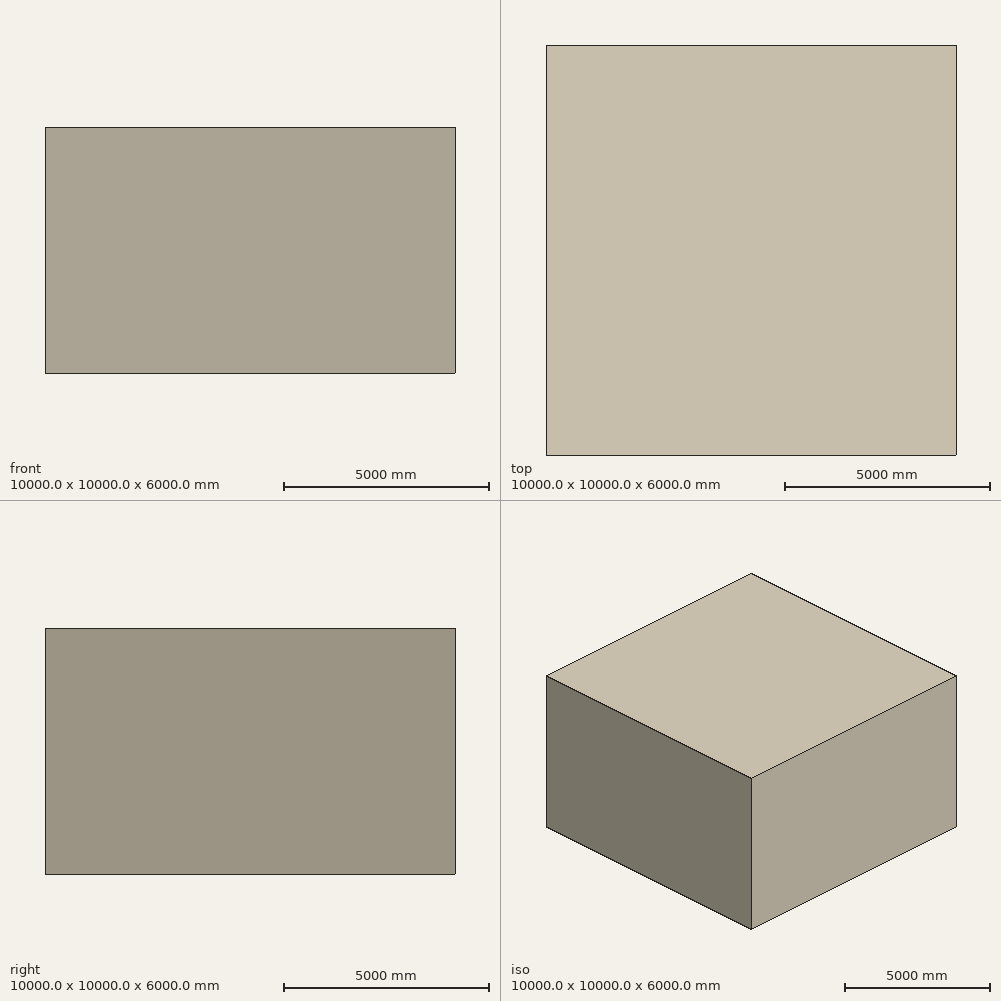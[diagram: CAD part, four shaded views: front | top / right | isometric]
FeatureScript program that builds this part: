
annotation { "Feature Type Name" : "Feature", "Feature Type Description" : "" }
export const myFeature = defineFeature(function(context is Context, id is Id, definition is map)
    precondition{}
    {
        {
            var Q0;
            Q0=qCreatedBy(makeId("Top.planeOp"),FACE);
            var sketch = newSketch(context, id + "F0", { "sketchPlane" : qUnion([Q0])});
            skLineSegment(sketch, "E0.bottom", {"start": v(-4986.23, 4988.21) * mm, "end": v(5013.77, 4988.21) * mm});
            skLineSegment(sketch, "E0.top", {"start": v(-4986.23, -5011.79) * mm, "end": v(5013.77, -5011.79) * mm});
            skLineSegment(sketch, "E0.left", {"start": v(-4986.23, 4988.21) * mm, "end": v(-4986.23, -5011.79) * mm});
            skLineSegment(sketch, "E0.right", {"start": v(5013.77, 4988.21) * mm, "end": v(5013.77, -5011.79) * mm});
            skSolve(sketch);
        }
        {
            var Q0;
            Q0 = qSketchRegion(id + "F0", true);
            extrude(context, id + "F1", {"entities" : qUnion([Q0]), "depth" : 6000 * mm, "offsetDistance" : 25.4 * mm});
        }
    });
